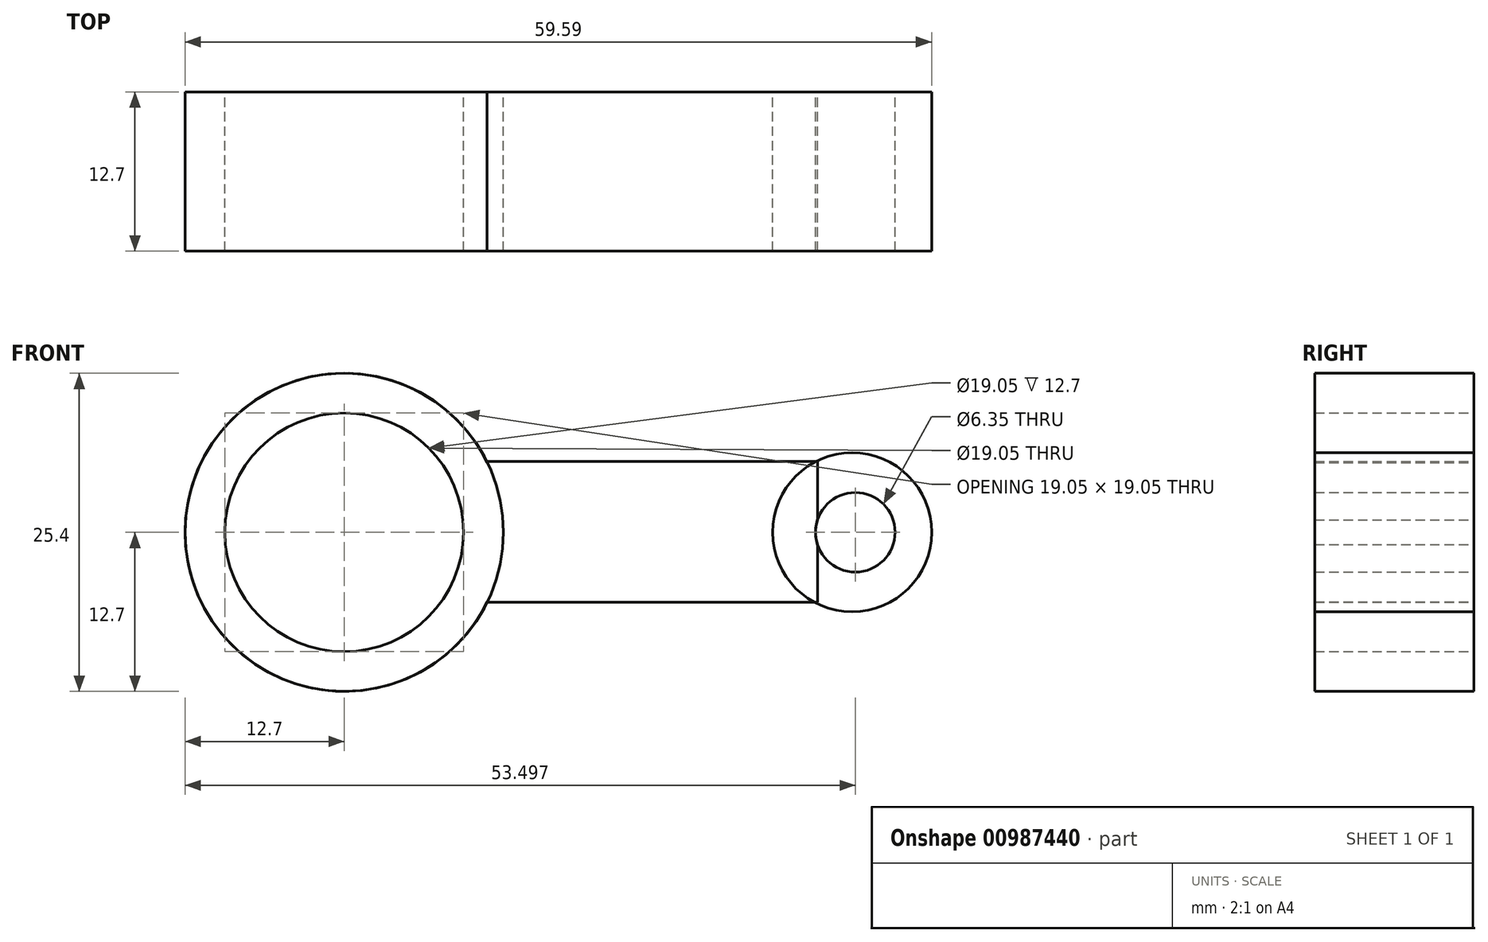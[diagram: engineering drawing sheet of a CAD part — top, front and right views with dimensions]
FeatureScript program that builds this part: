
annotation { "Feature Type Name" : "Feature", "Feature Type Description" : "" }
export const myFeature = defineFeature(function(context is Context, id is Id, definition is map)
    precondition{}
    {
        {
            var Q0;
            Q0=qCreatedBy(makeId("Front.planeOp"),FACE);
            var sketch = newSketch(context, id + "F0", { "sketchPlane" : qUnion([Q0])});
            skCircle(sketch, "E0", {"center": v(0, 0) * mm, "radius": 12.7 * mm});
            skCircle(sketch, "E1", {"center": v(40.54, 0) * mm, "radius": 6.35 * mm});
            skSolve(sketch);
        }
        {
            var Q0;
            Q0=makeQuery(id+"F0.imprint","IMPRINT",FACE,{"disambiguationData":[TD([[makeQuery(id+"F0.imprint","IMPRINT",EDGE,{"derivedFrom":sQuery(id+"F0.wireOp",EDGE,"E0")}),1.0]])]});
            var sketch = newSketch(context, id + "F1", { "sketchPlane" : qUnion([Q0])});
            skLineSegment(sketch, "E2.bottom", {"start": v(11.42, 5.65) * mm, "end": v(37.78, 5.65) * mm});
            skLineSegment(sketch, "E2.top", {"start": v(11.42, -5.6) * mm, "end": v(37.78, -5.6) * mm});
            skLineSegment(sketch, "E2.left", {"start": v(11.42, 5.65) * mm, "end": v(11.42, -5.6) * mm});
            skLineSegment(sketch, "E2.right", {"start": v(37.78, 5.65) * mm, "end": v(37.78, -5.6) * mm});
            skSolve(sketch);
        }
        {
            var Q0;
            Q0=qCreatedBy(makeId("Front.planeOp"),FACE);
            var sketch = newSketch(context, id + "F2", { "sketchPlane" : qUnion([Q0])});
            skCircle(sketch, "E3", {"center": v(0, 0) * mm, "radius": 9.53 * mm});
            skCircle(sketch, "E4", {"center": v(40.58, 0) * mm, "radius": 3.18 * mm});
            skSolve(sketch);
        }
        {
            var Q0;
            {var subQ0=sQuery(id+"F1.wireOp",EDGE,"E2.left");var subQ1=makeQuery(id+"F0.imprint","IMPRINT",EDGE,{"derivedFrom":sQuery(id+"F0.wireOp",EDGE,"E0")});var subQ2=makeQuery(id+"F1.imprint","INTERSECT",VERTEX,{"disambiguationData":[OD(0.0)],"derivedFrom":[subQ1,subQ0]});Q0=makeQuery(id+"F1.imprint","IMPRINT",FACE,{"disambiguationData":[TD([[makeQuery(id+"F1.imprint","IMPRINT",EDGE,{"disambiguationData":[TD([[subQ2,-1.0]])],"derivedFrom":subQ0}),1.0]])]});}
            var Q1;
            Q1=makeQuery(id+"F0.imprint","IMPRINT",FACE,{"disambiguationData":[TD([[makeQuery(id+"F0.imprint","IMPRINT",EDGE,{"derivedFrom":sQuery(id+"F0.wireOp",EDGE,"E1")}),1.0]])]});
            var Q2;
            Q2=makeQuery(id+"F2.imprint","IMPRINT",FACE,{"disambiguationData":[TD([[makeQuery(id+"F2.imprint","IMPRINT",EDGE,{"derivedFrom":sQuery(id+"F2.wireOp",EDGE,"E3")}),1.0]])]});
            var Q3;
            {var subQ4=sQuery(id+"F1.wireOp",EDGE,"E2.bottom");Q3=makeQuery(id+"F1.imprint","IMPRINT",FACE,{"disambiguationData":[TD([[makeQuery(id+"F1.imprint","IMPRINT",EDGE,{"derivedFrom":subQ4}),-1.0]])]});}
            var Q4;
            Q4=makeQuery(id+"F0.imprint","IMPRINT",FACE,{"disambiguationData":[TD([[makeQuery(id+"F0.imprint","IMPRINT",EDGE,{"derivedFrom":sQuery(id+"F0.wireOp",EDGE,"E0")}),1.0]])]});
            var Q5;
            {var subQ0=sQuery(id+"F1.wireOp",EDGE,"E2.left");var subQ1=makeQuery(id+"F0.imprint","IMPRINT",EDGE,{"derivedFrom":sQuery(id+"F0.wireOp",EDGE,"E0")});var subQ2=makeQuery(id+"F1.imprint","INTERSECT",VERTEX,{"disambiguationData":[OD(0.0)],"derivedFrom":[subQ1,subQ0]});Q5=makeQuery(id+"F1.imprint","IMPRINT",FACE,{"disambiguationData":[TD([[makeQuery(id+"F1.imprint","IMPRINT",EDGE,{"disambiguationData":[TD([[subQ2,-1.0]])],"derivedFrom":subQ0}),-1.0]])]});}
            extrude(context, id + "F3", {"entities" : qUnion([Q0, Q1, Q2, Q3, Q4, Q5]), "depth" : 12.7 * mm, "offsetDistance" : 25.4 * mm});
        }
        {
            var Q0;
            Q0=qCreatedBy(makeId("Front.planeOp"),FACE);
            var sketch = newSketch(context, id + "F4", { "sketchPlane" : qUnion([Q0])});
            skPoint(sketch, "E5", {"position": v(0, 0) * mm});
            skPoint(sketch, "E6", {"position": v(40.35, 0) * mm});
            skSolve(sketch);
        }
        {
            var Q0;
            Q0=sQuery(id+"F4.wireOp",VERTEX,"E5");
            var Q1;
            Q1=makeQuery(id+"F3.opExtrude","SWEPT_BODY",BODY,{"disambiguationData":[OSD([sQuery(id+"F0.wireOp",EDGE,"E0")])]});
            var Q2;
            Q2=makeQuery(id+"F3.opExtrude","SWEPT_BODY",BODY,{"disambiguationData":[OSD([sQuery(id+"F0.wireOp",EDGE,"E0"),sQuery(id+"F1.wireOp",EDGE,"E2.bottom"),sQuery(id+"F1.wireOp",EDGE,"E2.top"),sQuery(id+"F1.wireOp",EDGE,"E2.left"),sQuery(id+"F1.wireOp",EDGE,"E2.right")])]});
            var Q3;
            Q3=makeQuery(id+"F3.opExtrude","SWEPT_BODY",BODY,{"disambiguationData":[OSD([sQuery(id+"F2.wireOp",EDGE,"E3")])]});
            hole(context, id + "F5", {"style" : HoleStyle.SIMPLE, "endStyle" : HoleEndStyle.BLIND, "oppositeDirection" : true, "holeDiameter" : 19.05 * mm, "majorDiameter" : 6.35 * mm, "holeDepth" : 25.4 * mm, "isTappedThrough" : true, "tappedDepth" : 12.7 * mm, "tapClearance" : 3, "locations" : qUnion([Q0]), "scope" : qUnion([Q1, Q2, Q3])});
        }
        {
            var Q0;
            Q0=qCreatedBy(makeId("Front.planeOp"),FACE);
            var sketch = newSketch(context, id + "F6", { "sketchPlane" : qUnion([Q0])});
            skPoint(sketch, "E7", {"position": v(40.8, 0) * mm});
            skSolve(sketch);
        }
        {
            var Q0;
            Q0=sQuery(id+"F6.wireOp",VERTEX,"E7");
            var Q1;
            Q1=makeQuery(id+"F3.opExtrude","SWEPT_BODY",BODY,{"disambiguationData":[OSD([sQuery(id+"F0.wireOp",EDGE,"E0"),sQuery(id+"F1.wireOp",EDGE,"E2.bottom"),sQuery(id+"F1.wireOp",EDGE,"E2.top"),sQuery(id+"F1.wireOp",EDGE,"E2.left"),sQuery(id+"F1.wireOp",EDGE,"E2.right")])]});
            var Q2;
            Q2=makeQuery(id+"F3.opExtrude","SWEPT_BODY",BODY,{"disambiguationData":[OSD([sQuery(id+"F0.wireOp",EDGE,"E1")])]});
            hole(context, id + "F7", {"style" : HoleStyle.SIMPLE, "endStyle" : HoleEndStyle.BLIND, "oppositeDirection" : true, "holeDiameter" : 6.35 * mm, "majorDiameter" : 6.35 * mm, "holeDepth" : 12.7 * mm, "isTappedThrough" : true, "tappedDepth" : 12.7 * mm, "tapClearance" : 3, "locations" : qUnion([Q0]), "scope" : qUnion([Q1, Q2])});
        }
    });
